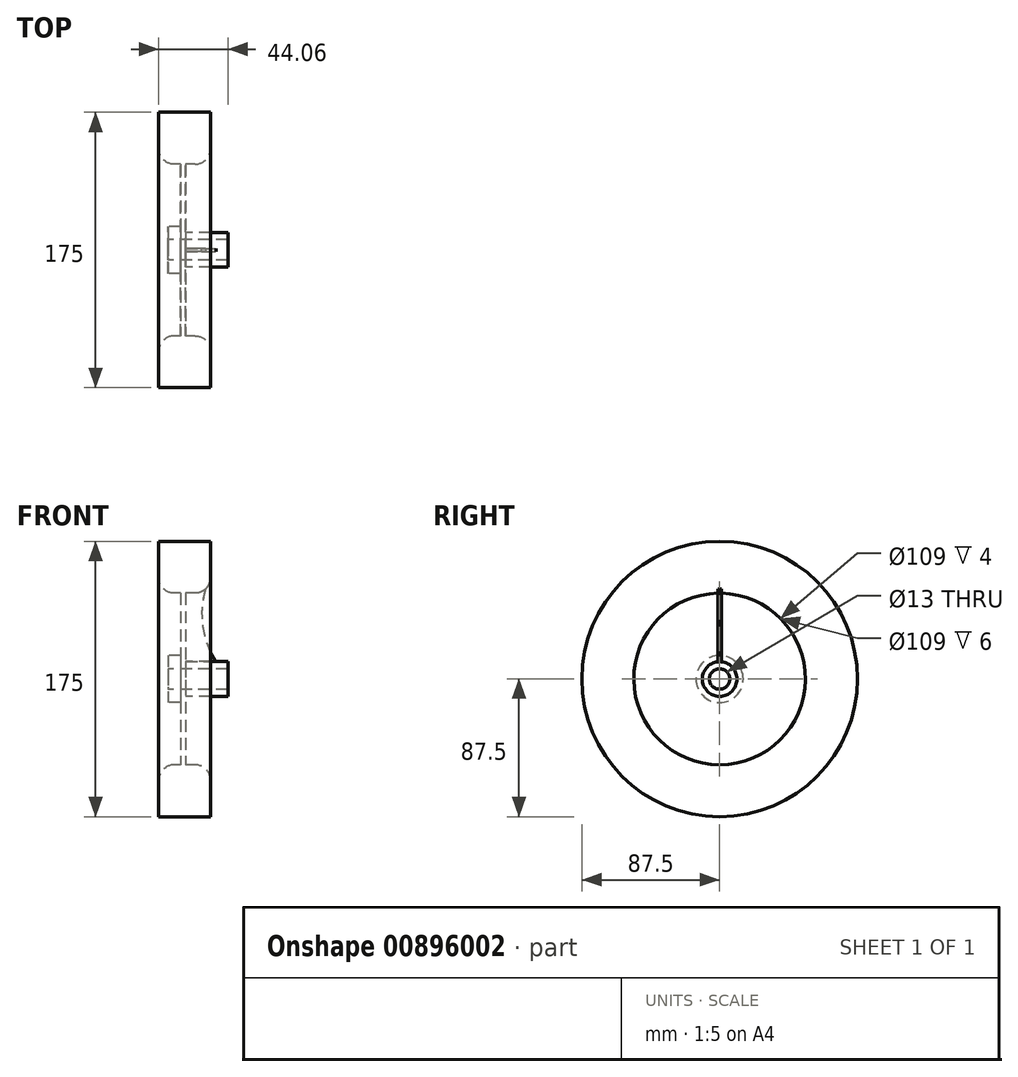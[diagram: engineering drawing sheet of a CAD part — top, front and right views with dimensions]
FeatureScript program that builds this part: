
annotation { "Feature Type Name" : "Feature", "Feature Type Description" : "" }
export const myFeature = defineFeature(function(context is Context, id is Id, definition is map)
    precondition{}
    {
        {
            var Q0;
            Q0=qCreatedBy(makeId("Top.planeOp"),FACE);
            var sketch = newSketch(context, id + "F0", { "sketchPlane" : qUnion([Q0])});
            skLineSegment(sketch, "E0", {"start": v(-69.33, 0) * mm, "end": v(65.9, 0) * mm, "construction": true});
            skSolve(sketch);
        }
        {
            var Q0;
            Q0=qCreatedBy(makeId("Front.planeOp"),FACE);
            var sketch = newSketch(context, id + "F1", { "sketchPlane" : qUnion([Q0])});
            skLineSegment(sketch, "E1", {"start": v(17.94, 87.5) * mm, "end": v(17.94, 54.5) * mm});
            skLineSegment(sketch, "E2", {"start": v(17.94, 54.5) * mm, "end": v(1.94, 54.5) * mm});
            skLineSegment(sketch, "E3", {"start": v(1.94, 54.5) * mm, "end": v(1.94, 11) * mm});
            skLineSegment(sketch, "E4", {"start": v(1.94, 11) * mm, "end": v(29, 11) * mm});
            skLineSegment(sketch, "E5", {"start": v(29, 11) * mm, "end": v(29, 6.5) * mm});
            skLineSegment(sketch, "E6", {"start": v(29, 6.5) * mm, "end": v(-9, 6.5) * mm});
            skLineSegment(sketch, "E7", {"start": v(-9, 6.5) * mm, "end": v(-9, 15) * mm});
            skLineSegment(sketch, "E8", {"start": v(-9, 15) * mm, "end": v(-1.06, 15) * mm});
            skLineSegment(sketch, "E9", {"start": v(17.94, 87.5) * mm, "end": v(-15.06, 87.5) * mm});
            skLineSegment(sketch, "E10", {"start": v(-15.06, 87.5) * mm, "end": v(-15.06, 54.5) * mm});
            skLineSegment(sketch, "E11", {"start": v(-15.06, 54.5) * mm, "end": v(-1.06, 54.5) * mm});
            skLineSegment(sketch, "E12", {"start": v(-1.06, 54.5) * mm, "end": v(-1.06, 15) * mm});
            skSolve(sketch);
        }
        {
            var Q0;
            Q0=makeQuery(id+"F1.imprint","IMPRINT",FACE,{"disambiguationData":[TD([[makeQuery(id+"F1.imprint","IMPRINT",EDGE,{"derivedFrom":sQuery(id+"F1.wireOp",EDGE,"E1")}),-1.0]])]});
            var Q1;
            Q1=sQuery(id+"F0.wireOp",EDGE,"E0");
            revolve(context, id + "F2", {"surfaceOperationType" : NewSurfaceOperationType.NEW, "entities" : qUnion([Q0]), "axis" : qUnion([Q1]), "revolveType" : RevolveType.FULL});
        }
        {
            var Q0;
            Q0=makeQuery(id+"F2.opRevolve","SWEPT_EDGE",EDGE,{"disambiguationData":[OSD([sQuery(id+"F1.wireOp",EDGE,"E1"),sQuery(id+"F1.wireOp",EDGE,"E2")])]});
            var Q1;
            Q1=makeQuery(id+"F2.opRevolve","SWEPT_EDGE",EDGE,{"disambiguationData":[OSD([sQuery(id+"F1.wireOp",EDGE,"E10"),sQuery(id+"F1.wireOp",EDGE,"E11")])]});
            fillet(context, id + "F3", {"entities" : qUnion([Q0, Q1]), "radius" : 10 * mm, "tangentPropagation" : true, "allowEdgeOverflow" : false});
        }
        {
            var Q0;
            Q0=qCreatedBy(makeId("Front.planeOp"),FACE);
            var sketch = newSketch(context, id + "F4", { "sketchPlane" : qUnion([Q0])});
            skArc(sketch, "E13", {"start": v(14.64, 57.1) * mm, "mid": v(12.87, 33.39) * mm, "end": v(21.26, 11.15) * mm});
            skLineSegment(sketch, "E14", {"start": v(14.64, 57.1) * mm, "end": v(2.09, 57.1) * mm});
            skLineSegment(sketch, "E15", {"start": v(2.09, 57.1) * mm, "end": v(2.09, 11.04) * mm});
            skLineSegment(sketch, "E16", {"start": v(2.09, 11.04) * mm, "end": v(21.26, 11.15) * mm});
            skSolve(sketch);
        }
        {
            var Q0;
            Q0 = qSketchRegion(id + "F4", true);
            extrude(context, id + "F5", {"entities" : qUnion([Q0]), "operationType" : NewBodyOperationType.ADD, "endBound" : BoundingType.SYMMETRIC, "depth" : 2 * mm, "offsetDistance" : 25.4 * mm});
        }
    });
